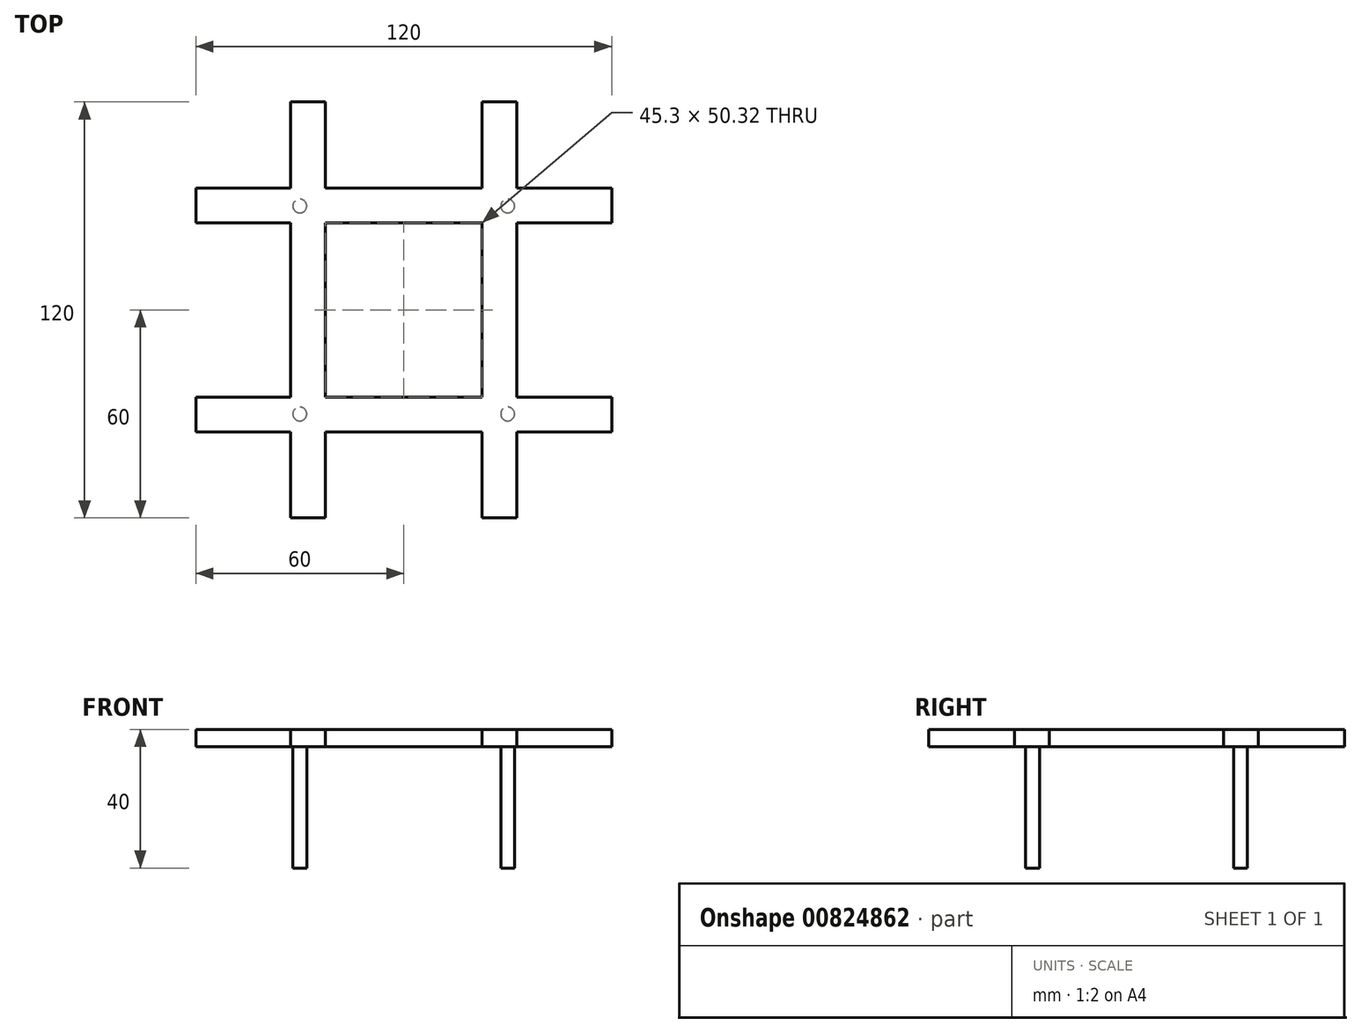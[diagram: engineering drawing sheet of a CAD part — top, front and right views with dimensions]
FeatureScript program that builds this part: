
annotation { "Feature Type Name" : "Feature", "Feature Type Description" : "" }
export const myFeature = defineFeature(function(context is Context, id is Id, definition is map)
    precondition{}
    {
        {
            var Q0;
            Q0=qCreatedBy(makeId("Top.planeOp"),FACE);
            var sketch = newSketch(context, id + "F0", { "sketchPlane" : qUnion([Q0])});
            skLineSegment(sketch, "E0.bottom", {"start": v(-60, 25.16) * mm, "end": v(60, 25.16) * mm});
            skLineSegment(sketch, "E0.top", {"start": v(-60, 35.16) * mm, "end": v(60, 35.16) * mm});
            skLineSegment(sketch, "E0.left", {"start": v(-60, 25.16) * mm, "end": v(-60, 35.16) * mm});
            skLineSegment(sketch, "E0.right", {"start": v(60, 25.16) * mm, "end": v(60, 35.16) * mm});
            skLineSegment(sketch, "E1.bottom", {"start": v(-22.65, -60) * mm, "end": v(-32.65, -60) * mm});
            skLineSegment(sketch, "E1.top", {"start": v(-22.65, 60) * mm, "end": v(-32.65, 60) * mm});
            skLineSegment(sketch, "E1.left", {"start": v(-22.65, -60) * mm, "end": v(-22.65, 60) * mm});
            skLineSegment(sketch, "E1.right", {"start": v(-32.65, -60) * mm, "end": v(-32.65, 60) * mm});
            skLineSegment(sketch, "E2.MirrorCS", {"start": v(22.65, 60) * mm, "end": v(32.65, 60) * mm});
            skLineSegment(sketch, "E3.MirrorCS", {"start": v(32.65, -60) * mm, "end": v(32.65, 60) * mm});
            skLineSegment(sketch, "E4.MirrorCS", {"start": v(22.65, -60) * mm, "end": v(22.65, 60) * mm});
            skLineSegment(sketch, "E5.MirrorCS", {"start": v(22.65, -60) * mm, "end": v(32.65, -60) * mm});
            skLineSegment(sketch, "E6.MirrorCS", {"start": v(-60, -25.16) * mm, "end": v(60, -25.16) * mm});
            skLineSegment(sketch, "E7.MirrorCS", {"start": v(-60, -35.16) * mm, "end": v(60, -35.16) * mm});
            skLineSegment(sketch, "E8.MirrorCS", {"start": v(60, -25.16) * mm, "end": v(60, -35.16) * mm});
            skLineSegment(sketch, "E9.MirrorCS", {"start": v(-60, -25.16) * mm, "end": v(-60, -35.16) * mm});
            skSolve(sketch);
        }
        {
            var Q0;
            {var subQ0=sQuery(id+"F0.wireOp",EDGE,"E0.left");Q0=makeQuery(id+"F0.imprint","IMPRINT",FACE,{"disambiguationData":[TD([[makeQuery(id+"F0.imprint","IMPRINT",EDGE,{"derivedFrom":subQ0}),-1.0]])]});}
            var Q1;
            {var subQ0=sQuery(id+"F0.wireOp",EDGE,"E1.right");var subQ1=sQuery(id+"F0.wireOp",EDGE,"E0.bottom");var subQ2=makeQuery(id+"F0.imprint","INTERSECT",VERTEX,{"derivedFrom":[subQ1,subQ0]});Q1=makeQuery(id+"F0.imprint","IMPRINT",FACE,{"disambiguationData":[TD([[makeQuery(id+"F0.imprint","IMPRINT",EDGE,{"disambiguationData":[TD([[subQ2,-1.0]])],"derivedFrom":subQ1}),1.0]])]});}
            var Q2;
            {var subQ5=sQuery(id+"F0.wireOp",EDGE,"E1.top");Q2=makeQuery(id+"F0.imprint","IMPRINT",FACE,{"disambiguationData":[TD([[makeQuery(id+"F0.imprint","IMPRINT",EDGE,{"derivedFrom":subQ5}),1.0]])]});}
            var Q3;
            {var subQ0=sQuery(id+"F0.wireOp",EDGE,"E1.left");var subQ1=sQuery(id+"F0.wireOp",EDGE,"E0.bottom");var subQ2=makeQuery(id+"F0.imprint","INTERSECT",VERTEX,{"derivedFrom":[subQ1,subQ0]});Q3=makeQuery(id+"F0.imprint","IMPRINT",FACE,{"disambiguationData":[TD([[makeQuery(id+"F0.imprint","IMPRINT",EDGE,{"disambiguationData":[TD([[subQ2,-1.0]])],"derivedFrom":subQ1}),1.0]])]});}
            var Q4;
            {var subQ0=sQuery(id+"F0.wireOp",EDGE,"E3.MirrorCS");var subQ1=sQuery(id+"F0.wireOp",EDGE,"E0.bottom");var subQ2=makeQuery(id+"F0.imprint","INTERSECT",VERTEX,{"derivedFrom":[subQ1,subQ0]});Q4=makeQuery(id+"F0.imprint","IMPRINT",FACE,{"disambiguationData":[TD([[makeQuery(id+"F0.imprint","IMPRINT",EDGE,{"disambiguationData":[TD([[subQ2,1.0]])],"derivedFrom":subQ1}),1.0]])]});}
            var Q5;
            {var subQ5=sQuery(id+"F0.wireOp",EDGE,"E2.MirrorCS");Q5=makeQuery(id+"F0.imprint","IMPRINT",FACE,{"disambiguationData":[TD([[makeQuery(id+"F0.imprint","IMPRINT",EDGE,{"derivedFrom":subQ5}),-1.0]])]});}
            var Q6;
            {var subQ0=sQuery(id+"F0.wireOp",EDGE,"E0.right");Q6=makeQuery(id+"F0.imprint","IMPRINT",FACE,{"disambiguationData":[TD([[makeQuery(id+"F0.imprint","IMPRINT",EDGE,{"derivedFrom":subQ0}),1.0]])]});}
            var Q7;
            {var subQ0=sQuery(id+"F0.wireOp",EDGE,"E3.MirrorCS");var subQ1=sQuery(id+"F0.wireOp",EDGE,"E0.bottom");var subQ2=makeQuery(id+"F0.imprint","INTERSECT",VERTEX,{"derivedFrom":[subQ1,subQ0]});Q7=makeQuery(id+"F0.imprint","IMPRINT",FACE,{"disambiguationData":[TD([[makeQuery(id+"F0.imprint","IMPRINT",EDGE,{"disambiguationData":[TD([[subQ2,1.0]])],"derivedFrom":subQ1}),-1.0]])]});}
            var Q8;
            {var subQ0=sQuery(id+"F0.wireOp",EDGE,"E7.MirrorCS");var subQ1=sQuery(id+"F0.wireOp",EDGE,"E3.MirrorCS");var subQ2=makeQuery(id+"F0.imprint","INTERSECT",VERTEX,{"derivedFrom":[subQ1,subQ0]});Q8=makeQuery(id+"F0.imprint","IMPRINT",FACE,{"disambiguationData":[TD([[makeQuery(id+"F0.imprint","IMPRINT",EDGE,{"disambiguationData":[TD([[subQ2,-1.0]])],"derivedFrom":subQ1}),1.0]])]});}
            var Q9;
            {var subQ5=sQuery(id+"F0.wireOp",EDGE,"E8.MirrorCS");Q9=makeQuery(id+"F0.imprint","IMPRINT",FACE,{"disambiguationData":[TD([[makeQuery(id+"F0.imprint","IMPRINT",EDGE,{"derivedFrom":subQ5}),-1.0]])]});}
            var Q10;
            {var subQ0=sQuery(id+"F0.wireOp",EDGE,"E5.MirrorCS");Q10=makeQuery(id+"F0.imprint","IMPRINT",FACE,{"disambiguationData":[TD([[makeQuery(id+"F0.imprint","IMPRINT",EDGE,{"derivedFrom":subQ0}),1.0]])]});}
            var Q11;
            {var subQ0=sQuery(id+"F0.wireOp",EDGE,"E7.MirrorCS");var subQ1=sQuery(id+"F0.wireOp",EDGE,"E1.left");var subQ2=makeQuery(id+"F0.imprint","INTERSECT",VERTEX,{"derivedFrom":[subQ1,subQ0]});Q11=makeQuery(id+"F0.imprint","IMPRINT",FACE,{"disambiguationData":[TD([[makeQuery(id+"F0.imprint","IMPRINT",EDGE,{"disambiguationData":[TD([[subQ2,-1.0]])],"derivedFrom":subQ1}),1.0]])]});}
            var Q12;
            {var subQ5=sQuery(id+"F0.wireOp",EDGE,"E9.MirrorCS");Q12=makeQuery(id+"F0.imprint","IMPRINT",FACE,{"disambiguationData":[TD([[makeQuery(id+"F0.imprint","IMPRINT",EDGE,{"derivedFrom":subQ5}),1.0]])]});}
            var Q13;
            {var subQ0=sQuery(id+"F0.wireOp",EDGE,"E7.MirrorCS");var subQ1=sQuery(id+"F0.wireOp",EDGE,"E1.left");var subQ2=makeQuery(id+"F0.imprint","INTERSECT",VERTEX,{"derivedFrom":[subQ1,subQ0]});Q13=makeQuery(id+"F0.imprint","IMPRINT",FACE,{"disambiguationData":[TD([[makeQuery(id+"F0.imprint","IMPRINT",EDGE,{"disambiguationData":[TD([[subQ2,-1.0]])],"derivedFrom":subQ1}),-1.0]])]});}
            var Q14;
            {var subQ0=sQuery(id+"F0.wireOp",EDGE,"E1.bottom");Q14=makeQuery(id+"F0.imprint","IMPRINT",FACE,{"disambiguationData":[TD([[makeQuery(id+"F0.imprint","IMPRINT",EDGE,{"derivedFrom":subQ0}),-1.0]])]});}
            var Q15;
            {var subQ0=sQuery(id+"F0.wireOp",EDGE,"E1.right");var subQ1=sQuery(id+"F0.wireOp",EDGE,"E0.bottom");var subQ2=makeQuery(id+"F0.imprint","INTERSECT",VERTEX,{"derivedFrom":[subQ1,subQ0]});Q15=makeQuery(id+"F0.imprint","IMPRINT",FACE,{"disambiguationData":[TD([[makeQuery(id+"F0.imprint","IMPRINT",EDGE,{"disambiguationData":[TD([[subQ2,-1.0]])],"derivedFrom":subQ1}),-1.0]])]});}
            extrude(context, id + "F1", {"entities" : qUnion([Q0, Q1, Q2, Q3, Q4, Q5, Q6, Q7, Q8, Q9, Q10, Q11, Q12, Q13, Q14, Q15]), "depth" : 5 * mm, "offsetDistance" : 25 * mm});
        }
        {
            var Q0;
            Q0=makeQuery(id+"F1.opExtrude","CAP_FACE",FACE,{"disambiguationData":[OSD([sQuery(id+"F0.wireOp",EDGE,"E0.bottom"),sQuery(id+"F0.wireOp",EDGE,"E0.top"),sQuery(id+"F0.wireOp",EDGE,"E0.left"),sQuery(id+"F0.wireOp",EDGE,"E0.right"),sQuery(id+"F0.wireOp",EDGE,"E1.bottom"),sQuery(id+"F0.wireOp",EDGE,"E1.top"),sQuery(id+"F0.wireOp",EDGE,"E1.left"),sQuery(id+"F0.wireOp",EDGE,"E1.right"),sQuery(id+"F0.wireOp",EDGE,"E2.MirrorCS"),sQuery(id+"F0.wireOp",EDGE,"E3.MirrorCS"),sQuery(id+"F0.wireOp",EDGE,"E4.MirrorCS"),sQuery(id+"F0.wireOp",EDGE,"E5.MirrorCS"),sQuery(id+"F0.wireOp",EDGE,"E6.MirrorCS"),sQuery(id+"F0.wireOp",EDGE,"E7.MirrorCS"),sQuery(id+"F0.wireOp",EDGE,"E8.MirrorCS"),sQuery(id+"F0.wireOp",EDGE,"E9.MirrorCS")])],"isStart":true});
            var sketch = newSketch(context, id + "F2", { "sketchPlane" : qUnion([Q0])});
            skCircle(sketch, "E10", {"center": v(-30, 30) * mm, "radius": 2 * mm});
            skCircle(sketch, "E11", {"center": v(30, 30) * mm, "radius": 2 * mm});
            skCircle(sketch, "E12", {"center": v(30, -30) * mm, "radius": 2 * mm});
            skCircle(sketch, "E13", {"center": v(-30, -30) * mm, "radius": 2 * mm});
            skSolve(sketch);
        }
        {
            var Q0;
            Q0=makeQuery(id+"F2.imprint","IMPRINT",FACE,{"disambiguationData":[TD([[makeQuery(id+"F2.imprint","IMPRINT",EDGE,{"derivedFrom":sQuery(id+"F2.wireOp",EDGE,"E10")}),1.0]])]});
            var Q1;
            Q1=makeQuery(id+"F2.imprint","IMPRINT",FACE,{"disambiguationData":[TD([[makeQuery(id+"F2.imprint","IMPRINT",EDGE,{"derivedFrom":sQuery(id+"F2.wireOp",EDGE,"E11")}),1.0]])]});
            var Q2;
            Q2=makeQuery(id+"F2.imprint","IMPRINT",FACE,{"disambiguationData":[TD([[makeQuery(id+"F2.imprint","IMPRINT",EDGE,{"derivedFrom":sQuery(id+"F2.wireOp",EDGE,"E12")}),1.0]])]});
            var Q3;
            Q3=makeQuery(id+"F2.imprint","IMPRINT",FACE,{"disambiguationData":[TD([[makeQuery(id+"F2.imprint","IMPRINT",EDGE,{"derivedFrom":sQuery(id+"F2.wireOp",EDGE,"E13")}),1.0]])]});
            extrude(context, id + "F3", {"entities" : qUnion([Q0, Q1, Q2, Q3]), "operationType" : NewBodyOperationType.ADD, "depth" : 35 * mm, "offsetDistance" : 25 * mm});
        }
    });
